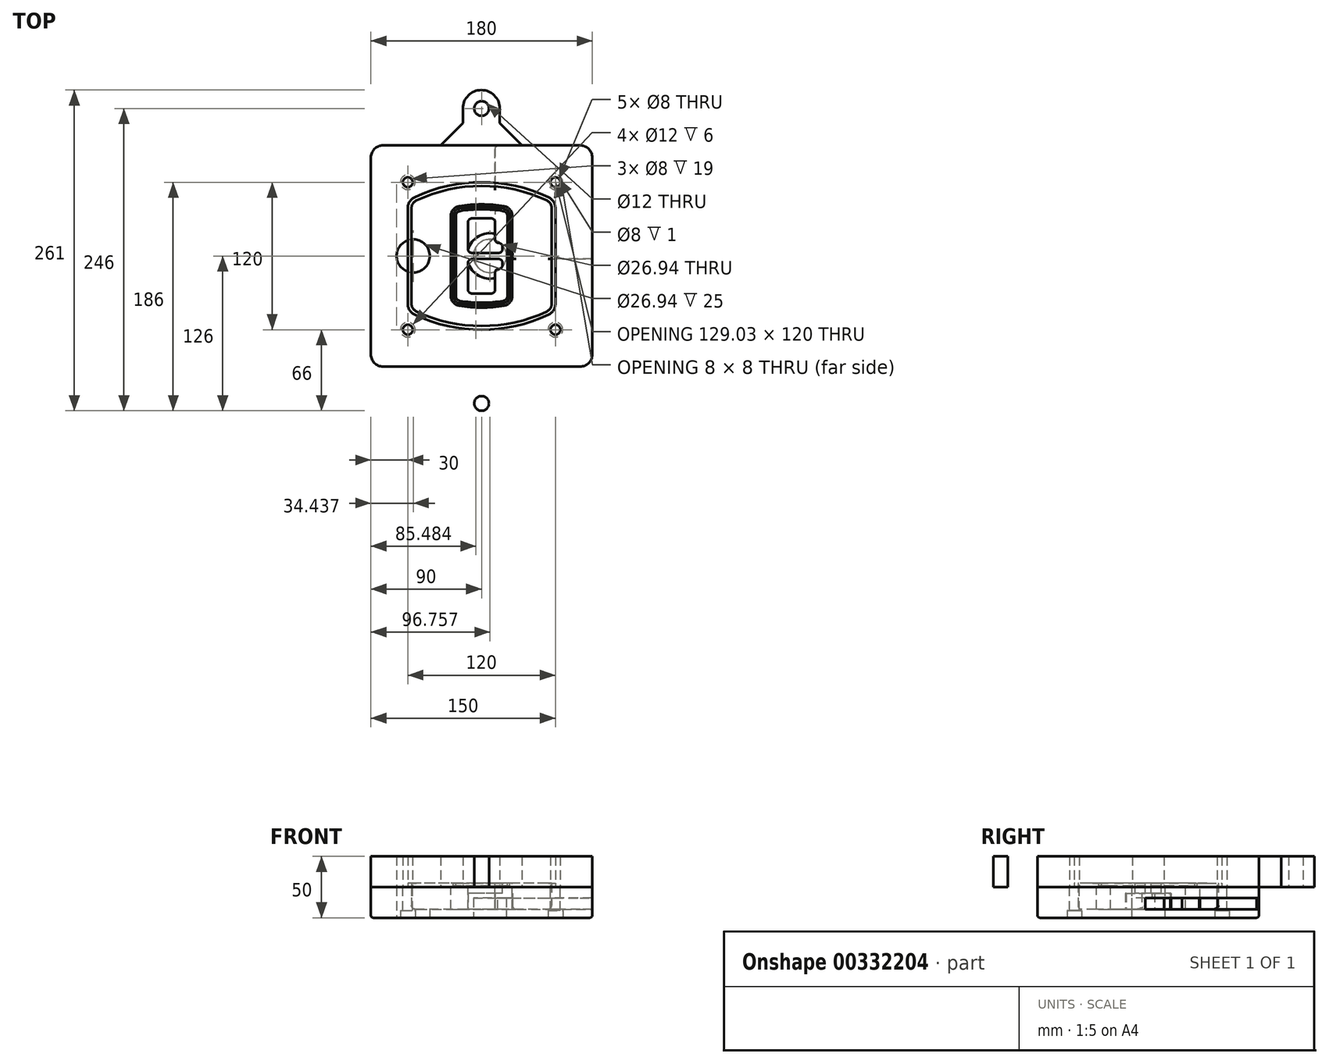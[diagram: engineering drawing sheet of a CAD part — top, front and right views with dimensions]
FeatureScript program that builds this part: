
annotation { "Feature Type Name" : "Feature", "Feature Type Description" : "" }
export const myFeature = defineFeature(function(context is Context, id is Id, definition is map)
    precondition{}
    {
        {
            var Q0;
            Q0=qCreatedBy(makeId("Top.planeOp"),FACE);
            var sketch = newSketch(context, id + "F0", { "sketchPlane" : qUnion([Q0])});
            skPoint(sketch, "E0.rect.middle", {"position": v(0, 0) * mm});
            skLineSegment(sketch, "E1.bottom", {"start": v(-80, -90) * mm, "end": v(80, -90) * mm});
            skLineSegment(sketch, "E1.top", {"start": v(-80, 90) * mm, "end": v(80, 90) * mm});
            skLineSegment(sketch, "E1.left", {"start": v(-90, -80) * mm, "end": v(-90, 80) * mm});
            skLineSegment(sketch, "E1.right", {"start": v(90, -80) * mm, "end": v(90, 80) * mm});
            skLineSegment(sketch, "E2", {"start": v(-90, 90) * mm, "end": v(90, -90) * mm, "construction": true});
            skLineSegment(sketch, "E3", {"start": v(90, 90) * mm, "end": v(-90, -90) * mm, "construction": true});
            skCircle(sketch, "E4", {"center": v(-60, 60) * mm, "radius": 4 * mm});
            skCircle(sketch, "E5", {"center": v(60, 60) * mm, "radius": 4 * mm});
            skCircle(sketch, "E6", {"center": v(60, -60) * mm, "radius": 4 * mm});
            skCircle(sketch, "E7", {"center": v(-60, -60) * mm, "radius": 4 * mm});
            skLineSegment(sketch, "E8", {"start": v(-60, 60) * mm, "end": v(60, 60) * mm, "construction": true});
            skLineSegment(sketch, "E9", {"start": v(60, 60) * mm, "end": v(60, -60) * mm, "construction": true});
            skLineSegment(sketch, "E10", {"start": v(60, -60) * mm, "end": v(-60, -60) * mm, "construction": true});
            skLineSegment(sketch, "E11", {"start": v(-60, -60) * mm, "end": v(-60, 60) * mm, "construction": true});
            skLineSegment(sketch, "E12", {"start": v(-60, 38.83) * mm, "end": v(-60, -38.83) * mm});
            skLineSegment(sketch, "E13", {"start": v(60, 38.83) * mm, "end": v(60, -38.83) * mm});
            skArc(sketch, "E14", {"start": v(54.26, 47.88) * mm, "mid": v(0, 60) * mm, "end": v(-54.26, 47.88) * mm});
            skArc(sketch, "E15", {"start": v(-54.26, -47.88) * mm, "mid": v(0, -60) * mm, "end": v(54.26, -47.88) * mm});
            skLineSegment(sketch, "E16", {"start": v(-60, 0) * mm, "end": v(60, 0) * mm, "construction": true});
            skPoint(sketch, "E17.visualSharp", {"position": v(-60, -45) * mm});
            skArc(sketch, "E17.filletArc", {"start": v(-60, -38.83) * mm, "mid": v(-58.44, -44.2) * mm, "end": v(-54.26, -47.88) * mm});
            skPoint(sketch, "E18.visualSharp", {"position": v(-60, 45) * mm});
            skArc(sketch, "E18.filletArc", {"start": v(-54.26, 47.88) * mm, "mid": v(-58.44, 44.2) * mm, "end": v(-60, 38.83) * mm});
            skPoint(sketch, "E19.visualSharp", {"position": v(60, 45) * mm});
            skArc(sketch, "E19.filletArc", {"start": v(60, 38.83) * mm, "mid": v(58.44, 44.2) * mm, "end": v(54.26, 47.88) * mm});
            skPoint(sketch, "E20.visualSharp", {"position": v(60, -45) * mm});
            skArc(sketch, "E20.filletArc", {"start": v(54.26, -47.88) * mm, "mid": v(58.44, -44.2) * mm, "end": v(60, -38.83) * mm});
            skPoint(sketch, "E21.visualSharp", {"position": v(-90, 90) * mm});
            skArc(sketch, "E21.filletArc", {"start": v(-80, 90) * mm, "mid": v(-87.07, 87.07) * mm, "end": v(-90, 80) * mm});
            skPoint(sketch, "E22.visualSharp", {"position": v(90, 90) * mm});
            skArc(sketch, "E22.filletArc", {"start": v(90, 80) * mm, "mid": v(87.07, 87.07) * mm, "end": v(80, 90) * mm});
            skPoint(sketch, "E23.visualSharp", {"position": v(90, -90) * mm});
            skArc(sketch, "E23.filletArc", {"start": v(80, -90) * mm, "mid": v(87.07, -87.07) * mm, "end": v(90, -80) * mm});
            skPoint(sketch, "E24.visualSharp", {"position": v(-90, -90) * mm});
            skArc(sketch, "E24.filletArc", {"start": v(-90, -80) * mm, "mid": v(-87.07, -87.07) * mm, "end": v(-80, -90) * mm});
            skArc(sketch, "E25.0", {"start": v(57, 38.83) * mm, "mid": v(55.9, 42.58) * mm, "end": v(52.98, 45.17) * mm});
            skLineSegment(sketch, "E25.1", {"start": v(57, 38.83) * mm, "end": v(57, -38.83) * mm});
            skArc(sketch, "E25.2", {"start": v(52.98, -45.17) * mm, "mid": v(55.9, -42.58) * mm, "end": v(57, -38.83) * mm});
            skArc(sketch, "E25.3", {"start": v(-52.98, -45.17) * mm, "mid": v(0, -57) * mm, "end": v(52.98, -45.17) * mm});
            skArc(sketch, "E25.4", {"start": v(-57, -38.83) * mm, "mid": v(-55.9, -42.58) * mm, "end": v(-52.98, -45.17) * mm});
            skArc(sketch, "E25.5", {"start": v(52.98, 45.17) * mm, "mid": v(0, 57) * mm, "end": v(-52.98, 45.17) * mm});
            skLineSegment(sketch, "E25.6", {"start": v(-57, 38.83) * mm, "end": v(-57, -38.83) * mm});
            skArc(sketch, "E25.7", {"start": v(-52.98, 45.17) * mm, "mid": v(-55.9, 42.58) * mm, "end": v(-57, 38.83) * mm});
            skArc(sketch, "E26.0", {"start": v(-55.96, 51.5) * mm, "mid": v(-61.82, 46.33) * mm, "end": v(-64, 38.83) * mm});
            skArc(sketch, "E26.1", {"start": v(55.96, 51.5) * mm, "mid": v(0, 64) * mm, "end": v(-55.96, 51.5) * mm});
            skArc(sketch, "E26.2", {"start": v(64, 38.83) * mm, "mid": v(61.82, 46.33) * mm, "end": v(55.96, 51.5) * mm});
            skLineSegment(sketch, "E26.3", {"start": v(64, 38.83) * mm, "end": v(64, -38.83) * mm});
            skArc(sketch, "E26.4", {"start": v(55.96, -51.5) * mm, "mid": v(61.82, -46.33) * mm, "end": v(64, -38.83) * mm});
            skLineSegment(sketch, "E26.5", {"start": v(-64, 38.83) * mm, "end": v(-64, -38.83) * mm});
            skArc(sketch, "E26.6", {"start": v(-55.96, -51.5) * mm, "mid": v(0, -64) * mm, "end": v(55.96, -51.5) * mm});
            skArc(sketch, "E26.7", {"start": v(-64, -38.83) * mm, "mid": v(-61.82, -46.33) * mm, "end": v(-55.96, -51.5) * mm});
            skSolve(sketch);
        }
        {
            var Q0;
            Q0=makeQuery(id+"F0.imprint","IMPRINT",FACE,{"disambiguationData":[TD([[makeQuery(id+"F0.imprint","IMPRINT",EDGE,{"derivedFrom":sQuery(id+"F0.wireOp",EDGE,"E1.bottom")}),1.0]])]});
            var Q1;
            Q1=makeQuery(id+"F0.imprint","IMPRINT",FACE,{"disambiguationData":[TD([[makeQuery(id+"F0.imprint","IMPRINT",EDGE,{"derivedFrom":sQuery(id+"F0.wireOp",EDGE,"E12")}),1.0]])]});
            var Q2;
            Q2=makeQuery(id+"F0.imprint","IMPRINT",FACE,{"disambiguationData":[TD([[makeQuery(id+"F0.imprint","IMPRINT",EDGE,{"derivedFrom":sQuery(id+"F0.wireOp",EDGE,"E25.0")}),1.0]])]});
            var Q3;
            Q3=makeQuery(id+"F0.imprint","IMPRINT",FACE,{"disambiguationData":[TD([[makeQuery(id+"F0.imprint","IMPRINT",EDGE,{"derivedFrom":sQuery(id+"F0.wireOp",EDGE,"E12")}),-1.0]])]});
            extrude(context, id + "F1", {"entities" : qUnion([Q0, Q1, Q2, Q3]), "oppositeDirection" : true, "depth" : 25 * mm});
        }
        {
            var Q0;
            Q0=makeQuery(id+"F0.imprint","IMPRINT",FACE,{"disambiguationData":[TD([[makeQuery(id+"F0.imprint","IMPRINT",EDGE,{"derivedFrom":sQuery(id+"F0.wireOp",EDGE,"E12")}),1.0]])]});
            extrude(context, id + "F2", {"entities" : qUnion([Q0]), "operationType" : NewBodyOperationType.ADD, "depth" : 3 * mm});
        }
        {
            var Q0;
            Q0=makeQuery(id+"F0.imprint","IMPRINT",FACE,{"disambiguationData":[TD([[makeQuery(id+"F0.imprint","IMPRINT",EDGE,{"derivedFrom":sQuery(id+"F0.wireOp",EDGE,"E25.0")}),1.0]])]});
            extrude(context, id + "F3", {"entities" : qUnion([Q0]), "operationType" : NewBodyOperationType.REMOVE, "oppositeDirection" : true, "depth" : 18 * mm});
        }
        {
            var Q0;
            Q0=makeQuery(id+"F2.opExtrude","CAP_FACE",FACE,{"disambiguationData":[OSD([sQuery(id+"F0.wireOp",EDGE,"E12"),sQuery(id+"F0.wireOp",EDGE,"E13"),sQuery(id+"F0.wireOp",EDGE,"E14"),sQuery(id+"F0.wireOp",EDGE,"E15"),sQuery(id+"F0.wireOp",EDGE,"E17.filletArc"),sQuery(id+"F0.wireOp",EDGE,"E18.filletArc"),sQuery(id+"F0.wireOp",EDGE,"E19.filletArc"),sQuery(id+"F0.wireOp",EDGE,"E20.filletArc"),sQuery(id+"F0.wireOp",EDGE,"E25.0"),sQuery(id+"F0.wireOp",EDGE,"E25.1"),sQuery(id+"F0.wireOp",EDGE,"E25.2"),sQuery(id+"F0.wireOp",EDGE,"E25.3"),sQuery(id+"F0.wireOp",EDGE,"E25.4"),sQuery(id+"F0.wireOp",EDGE,"E25.5"),sQuery(id+"F0.wireOp",EDGE,"E25.6"),sQuery(id+"F0.wireOp",EDGE,"E25.7")])],"isStart":false});
            var sketch = newSketch(context, id + "F4", { "sketchPlane" : qUnion([Q0])});
            skArc(sketch, "E27.0", {"start": v(-18.34, -40.45) * mm, "mid": v(0, -42) * mm, "end": v(18.34, -40.45) * mm});
            skArc(sketch, "E28.0", {"start": v(18.34, 40.45) * mm, "mid": v(0, 42) * mm, "end": v(-18.34, 40.45) * mm});
            skLineSegment(sketch, "E29", {"start": v(-25, 32.57) * mm, "end": v(-25, -32.57) * mm});
            skLineSegment(sketch, "E30", {"start": v(25, 32.57) * mm, "end": v(25, -32.57) * mm});
            skLineSegment(sketch, "E31", {"start": v(-25, 39.1) * mm, "end": v(25, 39.1) * mm, "construction": true});
            skLineSegment(sketch, "E32", {"start": v(-25, -39.1) * mm, "end": v(25, -39.1) * mm, "construction": true});
            skPoint(sketch, "E33.visualSharp", {"position": v(-25, 39.1) * mm});
            skArc(sketch, "E33.filletArc", {"start": v(-18.34, 40.45) * mm, "mid": v(-23.11, 37.73) * mm, "end": v(-25, 32.57) * mm});
            skPoint(sketch, "E34.visualSharp", {"position": v(25, 39.1) * mm});
            skArc(sketch, "E34.filletArc", {"start": v(25, 32.57) * mm, "mid": v(23.11, 37.73) * mm, "end": v(18.34, 40.45) * mm});
            skPoint(sketch, "E35.visualSharp", {"position": v(25, -39.1) * mm});
            skArc(sketch, "E35.filletArc", {"start": v(18.34, -40.45) * mm, "mid": v(23.11, -37.73) * mm, "end": v(25, -32.57) * mm});
            skPoint(sketch, "E36.visualSharp", {"position": v(-25, -39.1) * mm});
            skArc(sketch, "E36.filletArc", {"start": v(-25, -32.57) * mm, "mid": v(-23.11, -37.73) * mm, "end": v(-18.34, -40.45) * mm});
            skArc(sketch, "E37.0", {"start": v(52.98, 45.17) * mm, "mid": v(0, 57) * mm, "end": v(-52.98, 45.17) * mm});
            skArc(sketch, "E37.1", {"start": v(-52.98, 45.17) * mm, "mid": v(-55.9, 42.58) * mm, "end": v(-57, 38.83) * mm});
            skLineSegment(sketch, "E37.2", {"start": v(-57, 38.83) * mm, "end": v(-57, -38.83) * mm});
            skArc(sketch, "E37.3", {"start": v(-57, -38.83) * mm, "mid": v(-55.9, -42.58) * mm, "end": v(-52.98, -45.17) * mm});
            skArc(sketch, "E37.4", {"start": v(-52.98, -45.17) * mm, "mid": v(0, -57) * mm, "end": v(52.98, -45.17) * mm});
            skArc(sketch, "E37.5", {"start": v(52.98, -45.17) * mm, "mid": v(55.9, -42.58) * mm, "end": v(57, -38.83) * mm});
            skLineSegment(sketch, "E37.6", {"start": v(57, 38.83) * mm, "end": v(57, -38.83) * mm});
            skArc(sketch, "E37.7", {"start": v(57, 38.83) * mm, "mid": v(55.9, 42.58) * mm, "end": v(52.98, 45.17) * mm});
            skLineSegment(sketch, "E38.0", {"start": v(23, 32.57) * mm, "end": v(23, -32.57) * mm});
            skArc(sketch, "E38.1", {"start": v(18, -38.48) * mm, "mid": v(21.58, -36.44) * mm, "end": v(23, -32.57) * mm});
            skArc(sketch, "E38.2", {"start": v(-18, -38.48) * mm, "mid": v(0, -40) * mm, "end": v(18, -38.48) * mm});
            skArc(sketch, "E38.3", {"start": v(-23, -32.57) * mm, "mid": v(-21.58, -36.44) * mm, "end": v(-18, -38.48) * mm});
            skLineSegment(sketch, "E38.4", {"start": v(-23, 32.57) * mm, "end": v(-23, -32.57) * mm});
            skArc(sketch, "E38.5", {"start": v(23, 32.57) * mm, "mid": v(21.58, 36.44) * mm, "end": v(18, 38.48) * mm});
            skArc(sketch, "E38.6", {"start": v(-18, 38.48) * mm, "mid": v(-21.58, 36.44) * mm, "end": v(-23, 32.57) * mm});
            skArc(sketch, "E38.7", {"start": v(18, 38.48) * mm, "mid": v(0, 40) * mm, "end": v(-18, 38.48) * mm});
            skArc(sketch, "E39.0", {"start": v(21, 32.57) * mm, "mid": v(20.06, 35.15) * mm, "end": v(17.67, 36.5) * mm});
            skLineSegment(sketch, "E39.1", {"start": v(21, 32.57) * mm, "end": v(21, -32.57) * mm});
            skArc(sketch, "E39.2", {"start": v(17.67, -36.5) * mm, "mid": v(20.06, -35.15) * mm, "end": v(21, -32.57) * mm});
            skArc(sketch, "E39.3", {"start": v(-17.67, -36.5) * mm, "mid": v(0, -38) * mm, "end": v(17.67, -36.5) * mm});
            skArc(sketch, "E39.4", {"start": v(-21, -32.57) * mm, "mid": v(-20.06, -35.15) * mm, "end": v(-17.67, -36.5) * mm});
            skArc(sketch, "E39.5", {"start": v(17.67, 36.5) * mm, "mid": v(0, 38) * mm, "end": v(-17.67, 36.5) * mm});
            skLineSegment(sketch, "E39.6", {"start": v(-21, 32.57) * mm, "end": v(-21, -32.57) * mm});
            skArc(sketch, "E39.7", {"start": v(-17.67, 36.5) * mm, "mid": v(-20.06, 35.15) * mm, "end": v(-21, 32.57) * mm});
            skLineSegment(sketch, "E40", {"start": v(-25, 0) * mm, "end": v(25, 0) * mm, "construction": true});
            skLineSegment(sketch, "E41", {"start": v(-11, 5.5) * mm, "end": v(-11, 27.5) * mm});
            skLineSegment(sketch, "E42", {"start": v(-8, 30.5) * mm, "end": v(8, 30.5) * mm});
            skLineSegment(sketch, "E43", {"start": v(11, 27.5) * mm, "end": v(11, 13.5) * mm});
            skLineSegment(sketch, "E44", {"start": v(14, 10.5) * mm, "end": v(14, 10.5) * mm});
            skLineSegment(sketch, "E45", {"start": v(17, 7.5) * mm, "end": v(17, 5.5) * mm});
            skLineSegment(sketch, "E46", {"start": v(14, 2.5) * mm, "end": v(-8, 2.5) * mm});
            skPoint(sketch, "E47.visualSharp", {"position": v(-11, 30.5) * mm});
            skArc(sketch, "E47.filletArc", {"start": v(-8, 30.5) * mm, "mid": v(-10.12, 29.62) * mm, "end": v(-11, 27.5) * mm});
            skPoint(sketch, "E48.visualSharp", {"position": v(11, 30.5) * mm});
            skArc(sketch, "E48.filletArc", {"start": v(11, 27.5) * mm, "mid": v(10.12, 29.62) * mm, "end": v(8, 30.5) * mm});
            skPoint(sketch, "E49.visualSharp", {"position": v(11, 10.5) * mm});
            skArc(sketch, "E49.filletArc", {"start": v(11, 13.5) * mm, "mid": v(11.88, 11.38) * mm, "end": v(14, 10.5) * mm});
            skPoint(sketch, "E50.visualSharp", {"position": v(17, 10.5) * mm});
            skArc(sketch, "E50.filletArc", {"start": v(17, 7.5) * mm, "mid": v(16.12, 9.62) * mm, "end": v(14, 10.5) * mm});
            skPoint(sketch, "E51.visualSharp", {"position": v(17, 2.5) * mm});
            skArc(sketch, "E51.filletArc", {"start": v(14, 2.5) * mm, "mid": v(16.12, 3.38) * mm, "end": v(17, 5.5) * mm});
            skPoint(sketch, "E52.visualSharp", {"position": v(-11, 2.5) * mm});
            skArc(sketch, "E52.filletArc", {"start": v(-11, 5.5) * mm, "mid": v(-10.12, 3.38) * mm, "end": v(-8, 2.5) * mm});
            skLineSegment(sketch, "E53.0.MirrorCS", {"start": v(14, -2.5) * mm, "end": v(-8, -2.5) * mm});
            skArc(sketch, "E54.0.MirrorCS", {"start": v(-11, -5.5) * mm, "mid": v(-10.12, -3.38) * mm, "end": v(-8, -2.5) * mm});
            skLineSegment(sketch, "E55.0.MirrorCS", {"start": v(-11, -5.5) * mm, "end": v(-11, -27.5) * mm});
            skArc(sketch, "E56.0.MirrorCS", {"start": v(-8, -30.5) * mm, "mid": v(-10.12, -29.62) * mm, "end": v(-11, -27.5) * mm});
            skLineSegment(sketch, "E57.0.MirrorCS", {"start": v(-8, -30.5) * mm, "end": v(8, -30.5) * mm});
            skArc(sketch, "E58.0.MirrorCS", {"start": v(11, -27.5) * mm, "mid": v(10.12, -29.62) * mm, "end": v(8, -30.5) * mm});
            skLineSegment(sketch, "E59.0.MirrorCS", {"start": v(11, -27.5) * mm, "end": v(11, -13.5) * mm});
            skArc(sketch, "E60.0.MirrorCS", {"start": v(11, -13.5) * mm, "mid": v(11.88, -11.38) * mm, "end": v(14, -10.5) * mm});
            skArc(sketch, "E61.0.MirrorCS", {"start": v(17, -7.5) * mm, "mid": v(16.12, -9.62) * mm, "end": v(14, -10.5) * mm});
            skLineSegment(sketch, "E62.0.MirrorCS", {"start": v(17, -7.5) * mm, "end": v(17, -5.5) * mm});
            skArc(sketch, "E63.0.MirrorCS", {"start": v(14, -2.5) * mm, "mid": v(16.12, -3.38) * mm, "end": v(17, -5.5) * mm});
            skSolve(sketch);
        }
        {
            var Q0;
            Q0=makeQuery(id+"F4.imprint","IMPRINT",FACE,{"disambiguationData":[TD([[makeQuery(id+"F4.imprint","IMPRINT",EDGE,{"derivedFrom":sQuery(id+"F4.wireOp",EDGE,"E27.0")}),1.0]])]});
            var Q1;
            Q1=makeQuery(id+"F4.imprint","IMPRINT",FACE,{"disambiguationData":[TD([[makeQuery(id+"F4.imprint","IMPRINT",EDGE,{"derivedFrom":sQuery(id+"F4.wireOp",EDGE,"E38.0")}),-1.0]])]});
            var Q2;
            Q2=makeQuery(id+"F4.imprint","IMPRINT",FACE,{"disambiguationData":[TD([[makeQuery(id+"F4.imprint","IMPRINT",EDGE,{"derivedFrom":sQuery(id+"F4.wireOp",EDGE,"E39.0")}),1.0]])]});
            extrude(context, id + "F5", {"entities" : qUnion([Q0, Q1, Q2]), "operationType" : NewBodyOperationType.ADD, "endBound" : BoundingType.UP_TO_NEXT, "oppositeDirection" : true, "depth" : 25 * mm});
        }
        {
            var Q0;
            Q0=makeQuery(id+"F4.imprint","IMPRINT",FACE,{"disambiguationData":[TD([[makeQuery(id+"F4.imprint","IMPRINT",EDGE,{"derivedFrom":sQuery(id+"F4.wireOp",EDGE,"E38.0")}),-1.0]])]});
            extrude(context, id + "F6", {"entities" : qUnion([Q0]), "operationType" : NewBodyOperationType.REMOVE, "oppositeDirection" : true, "depth" : 2 * mm});
        }
        {
            var Q0;
            Q0=makeQuery(id+"F1.opExtrude","CAP_FACE",FACE,{"disambiguationData":[OSD([sQuery(id+"F0.wireOp",EDGE,"E1.bottom"),sQuery(id+"F0.wireOp",EDGE,"E1.top"),sQuery(id+"F0.wireOp",EDGE,"E1.left"),sQuery(id+"F0.wireOp",EDGE,"E1.right"),sQuery(id+"F0.wireOp",EDGE,"E4"),sQuery(id+"F0.wireOp",EDGE,"E5"),sQuery(id+"F0.wireOp",EDGE,"E6"),sQuery(id+"F0.wireOp",EDGE,"E7"),sQuery(id+"F0.wireOp",EDGE,"E21.filletArc"),sQuery(id+"F0.wireOp",EDGE,"E22.filletArc"),sQuery(id+"F0.wireOp",EDGE,"E23.filletArc"),sQuery(id+"F0.wireOp",EDGE,"E24.filletArc")])],"isStart":false});
            var sketch = newSketch(context, id + "F7", { "sketchPlane" : qUnion([Q0])});
            skCircle(sketch, "E64", {"center": v(6.76, 0) * mm, "radius": 13.47 * mm});
            skCircle(sketch, "E65", {"center": v(-55.56, 0) * mm, "radius": 13.47 * mm});
            skLineSegment(sketch, "E66", {"start": v(90, 0) * mm, "end": v(-90, 0) * mm});
            skCircle(sketch, "E67", {"center": v(6.76, 0) * mm, "radius": 18.47 * mm});
            skCircle(sketch, "E68", {"center": v(60, -60) * mm, "radius": 6 * mm});
            skCircle(sketch, "E69", {"center": v(-60, -60) * mm, "radius": 6 * mm});
            skCircle(sketch, "E70", {"center": v(-60, 60) * mm, "radius": 6 * mm});
            skCircle(sketch, "E71", {"center": v(60, 60) * mm, "radius": 6 * mm});
            skSolve(sketch);
        }
        {
            var Q0;
            {var subQ1=sQuery(id+"F7.wireOp",EDGE,"E66");var subQ4=sQuery(id+"F7.wireOp",EDGE,"E64");var subQ6=makeQuery(id+"F7.imprint","INTERSECT",VERTEX,{"disambiguationData":[OD(0.0)],"derivedFrom":[subQ4,subQ1]});Q0=makeQuery(id+"F7.imprint","IMPRINT",FACE,{"disambiguationData":[TD([[makeQuery(id+"F7.imprint","IMPRINT",EDGE,{"disambiguationData":[TD([[subQ6,-1.0]])],"derivedFrom":subQ4}),-1.0]])]});}
            var Q1;
            {var subQ0=sQuery(id+"F7.wireOp",EDGE,"E66");var subQ1=sQuery(id+"F7.wireOp",EDGE,"E64");var subQ3=makeQuery(id+"F7.imprint","INTERSECT",VERTEX,{"disambiguationData":[OD(0.0)],"derivedFrom":[subQ1,subQ0]});Q1=makeQuery(id+"F7.imprint","IMPRINT",FACE,{"disambiguationData":[TD([[makeQuery(id+"F7.imprint","IMPRINT",EDGE,{"disambiguationData":[TD([[subQ3,-1.0]])],"derivedFrom":subQ1}),1.0]])]});}
            var Q2;
            {var subQ0=sQuery(id+"F7.wireOp",EDGE,"E66");var subQ1=sQuery(id+"F7.wireOp",EDGE,"E64");var subQ3=makeQuery(id+"F7.imprint","INTERSECT",VERTEX,{"disambiguationData":[OD(0.0)],"derivedFrom":[subQ1,subQ0]});Q2=makeQuery(id+"F7.imprint","IMPRINT",FACE,{"disambiguationData":[TD([[makeQuery(id+"F7.imprint","IMPRINT",EDGE,{"disambiguationData":[TD([[subQ3,1.0]])],"derivedFrom":subQ1}),1.0]])]});}
            var Q3;
            {var subQ1=sQuery(id+"F7.wireOp",EDGE,"E66");var subQ4=sQuery(id+"F7.wireOp",EDGE,"E64");var subQ6=makeQuery(id+"F7.imprint","INTERSECT",VERTEX,{"disambiguationData":[OD(0.0)],"derivedFrom":[subQ4,subQ1]});Q3=makeQuery(id+"F7.imprint","IMPRINT",FACE,{"disambiguationData":[TD([[makeQuery(id+"F7.imprint","IMPRINT",EDGE,{"disambiguationData":[TD([[subQ6,1.0]])],"derivedFrom":subQ4}),-1.0]])]});}
            extrude(context, id + "F8", {"entities" : qUnion([Q0, Q1, Q2, Q3]), "operationType" : NewBodyOperationType.ADD, "oppositeDirection" : true, "depth" : 20 * mm});
        }
        {
            var Q0;
            {var subQ0=sQuery(id+"F7.wireOp",EDGE,"E66");var subQ1=sQuery(id+"F7.wireOp",EDGE,"E64");var subQ3=makeQuery(id+"F7.imprint","INTERSECT",VERTEX,{"disambiguationData":[OD(0.0)],"derivedFrom":[subQ1,subQ0]});Q0=makeQuery(id+"F7.imprint","IMPRINT",FACE,{"disambiguationData":[TD([[makeQuery(id+"F7.imprint","IMPRINT",EDGE,{"disambiguationData":[TD([[subQ3,-1.0]])],"derivedFrom":subQ1}),1.0]])]});}
            var Q1;
            {var subQ0=sQuery(id+"F7.wireOp",EDGE,"E66");var subQ1=sQuery(id+"F7.wireOp",EDGE,"E64");var subQ3=makeQuery(id+"F7.imprint","INTERSECT",VERTEX,{"disambiguationData":[OD(0.0)],"derivedFrom":[subQ1,subQ0]});Q1=makeQuery(id+"F7.imprint","IMPRINT",FACE,{"disambiguationData":[TD([[makeQuery(id+"F7.imprint","IMPRINT",EDGE,{"disambiguationData":[TD([[subQ3,1.0]])],"derivedFrom":subQ1}),1.0]])]});}
            extrude(context, id + "F9", {"entities" : qUnion([Q0, Q1]), "operationType" : NewBodyOperationType.REMOVE, "oppositeDirection" : true, "depth" : 16 * mm});
        }
        {
            var Q0;
            {var subQ0=sQuery(id+"F7.wireOp",EDGE,"E66");var subQ1=sQuery(id+"F7.wireOp",EDGE,"E65");var subQ3=makeQuery(id+"F7.imprint","INTERSECT",VERTEX,{"disambiguationData":[OD(0.0)],"derivedFrom":[subQ1,subQ0]});Q0=makeQuery(id+"F7.imprint","IMPRINT",FACE,{"disambiguationData":[TD([[makeQuery(id+"F7.imprint","IMPRINT",EDGE,{"disambiguationData":[TD([[subQ3,-1.0]])],"derivedFrom":subQ1}),1.0]])]});}
            var Q1;
            {var subQ0=sQuery(id+"F7.wireOp",EDGE,"E66");var subQ1=sQuery(id+"F7.wireOp",EDGE,"E65");var subQ3=makeQuery(id+"F7.imprint","INTERSECT",VERTEX,{"disambiguationData":[OD(0.0)],"derivedFrom":[subQ1,subQ0]});Q1=makeQuery(id+"F7.imprint","IMPRINT",FACE,{"disambiguationData":[TD([[makeQuery(id+"F7.imprint","IMPRINT",EDGE,{"disambiguationData":[TD([[subQ3,1.0]])],"derivedFrom":subQ1}),1.0]])]});}
            extrude(context, id + "F10", {"entities" : qUnion([Q0, Q1]), "operationType" : NewBodyOperationType.REMOVE, "oppositeDirection" : true, "depth" : 25 * mm});
        }
        {
            var Q0;
            Q0=makeQuery(id+"F7.imprint","IMPRINT",FACE,{"disambiguationData":[TD([[makeQuery(id+"F7.imprint","IMPRINT",EDGE,{"derivedFrom":sQuery(id+"F7.wireOp",EDGE,"E68")}),1.0]])]});
            var Q1;
            Q1=makeQuery(id+"F7.imprint","IMPRINT",FACE,{"disambiguationData":[TD([[makeQuery(id+"F7.imprint","IMPRINT",EDGE,{"derivedFrom":makeQuery(id+"F1.opExtrude","CAP_EDGE",EDGE,{"disambiguationData":[OSD([sQuery(id+"F0.wireOp",EDGE,"E5")])],"isStart":false})}),-1.0]])]});
            var Q2;
            Q2=makeQuery(id+"F7.imprint","IMPRINT",FACE,{"disambiguationData":[TD([[makeQuery(id+"F7.imprint","IMPRINT",EDGE,{"derivedFrom":sQuery(id+"F7.wireOp",EDGE,"E69")}),1.0]])]});
            var Q3;
            Q3=makeQuery(id+"F7.imprint","IMPRINT",FACE,{"disambiguationData":[TD([[makeQuery(id+"F7.imprint","IMPRINT",EDGE,{"derivedFrom":makeQuery(id+"F1.opExtrude","CAP_EDGE",EDGE,{"disambiguationData":[OSD([sQuery(id+"F0.wireOp",EDGE,"E4")])],"isStart":false})}),-1.0]])]});
            var Q4;
            Q4=makeQuery(id+"F7.imprint","IMPRINT",FACE,{"disambiguationData":[TD([[makeQuery(id+"F7.imprint","IMPRINT",EDGE,{"derivedFrom":sQuery(id+"F7.wireOp",EDGE,"E70")}),1.0]])]});
            var Q5;
            Q5=makeQuery(id+"F7.imprint","IMPRINT",FACE,{"disambiguationData":[TD([[makeQuery(id+"F7.imprint","IMPRINT",EDGE,{"derivedFrom":makeQuery(id+"F1.opExtrude","CAP_EDGE",EDGE,{"disambiguationData":[OSD([sQuery(id+"F0.wireOp",EDGE,"E7")])],"isStart":false})}),-1.0]])]});
            var Q6;
            Q6=makeQuery(id+"F7.imprint","IMPRINT",FACE,{"disambiguationData":[TD([[makeQuery(id+"F7.imprint","IMPRINT",EDGE,{"derivedFrom":sQuery(id+"F7.wireOp",EDGE,"E71")}),1.0]])]});
            var Q7;
            Q7=makeQuery(id+"F7.imprint","IMPRINT",FACE,{"disambiguationData":[TD([[makeQuery(id+"F7.imprint","IMPRINT",EDGE,{"derivedFrom":makeQuery(id+"F1.opExtrude","CAP_EDGE",EDGE,{"disambiguationData":[OSD([sQuery(id+"F0.wireOp",EDGE,"E6")])],"isStart":false})}),-1.0]])]});
            extrude(context, id + "F11", {"entities" : qUnion([Q0, Q1, Q2, Q3, Q4, Q5, Q6, Q7]), "operationType" : NewBodyOperationType.REMOVE, "oppositeDirection" : true, "depth" : 6 * mm});
        }
        {
            var Q0;
            Q0=makeQuery(id+"F9.boolean.opBoolean","COPY",FACE,{"derivedFrom":makeQuery(id+"F9.opExtrude","CAP_FACE",FACE,{"disambiguationData":[OSD([sQuery(id+"F7.wireOp",EDGE,"E64")])],"isStart":false})});
            var sketch = newSketch(context, id + "F12", { "sketchPlane" : qUnion([Q0])});
            skArc(sketch, "E72.0", {"start": v(11, -88.19) * mm, "mid": v(97.1, -83.6) * mm, "end": v(92.5, 2.5) * mm});
            skLineSegment(sketch, "E72.1", {"start": v(11, -17.97) * mm, "end": v(11, -17.97) * mm});
            skLineSegment(sketch, "E73", {"start": v(92.5, -105.13) * mm, "end": v(102.3, -105.13) * mm});
            skLineSegment(sketch, "E74.0", {"start": v(92.5, 2.5) * mm, "end": v(14, 2.5) * mm});
            skArc(sketch, "E74.1", {"start": v(14, 2.5) * mm, "mid": v(16.12, 3.38) * mm, "end": v(17, 5.5) * mm});
            skLineSegment(sketch, "E74.2", {"start": v(17, 7.5) * mm, "end": v(17, 5.5) * mm});
            skArc(sketch, "E74.3", {"start": v(17, 7.5) * mm, "mid": v(16.12, 9.62) * mm, "end": v(14, 10.5) * mm});
            skArc(sketch, "E74.4", {"start": v(11, 13.5) * mm, "mid": v(11.88, 11.38) * mm, "end": v(14, 10.5) * mm});
            skLineSegment(sketch, "E74.5", {"start": v(11, 13.5) * mm, "end": v(11, -88.19) * mm});
            skLineSegment(sketch, "E74.7", {"start": v(92.5, -2.5) * mm, "end": v(14, -2.5) * mm});
            skArc(sketch, "E74.8", {"start": v(14, -2.5) * mm, "mid": v(16.12, -3.38) * mm, "end": v(17, -5.5) * mm});
            skLineSegment(sketch, "E74.9", {"start": v(17, -7.5) * mm, "end": v(17, -5.5) * mm});
            skArc(sketch, "E74.10", {"start": v(17, -7.5) * mm, "mid": v(16.12, -9.62) * mm, "end": v(14, -10.5) * mm});
            skArc(sketch, "E74.11", {"start": v(11, -13.5) * mm, "mid": v(11.88, -11.38) * mm, "end": v(14, -10.5) * mm});
            skLineSegment(sketch, "E74.12", {"start": v(11, -17.97) * mm, "end": v(11, -13.5) * mm});
            skPoint(sketch, "E75.orphan", {"position": v(11, -27.5) * mm});
            skPoint(sketch, "E76.orphan", {"position": v(-8, -2.5) * mm});
            skPoint(sketch, "E77.orphan", {"position": v(-8, 2.5) * mm});
            skPoint(sketch, "E78.orphan", {"position": v(11, 27.5) * mm});
            skSolve(sketch);
        }
        {
            var Q0;
            {var subQ7=sQuery(id+"F12.wireOp",EDGE,"E72.0");var subQ14=sQuery(id+"F12.wireOp",EDGE,"E72.1");var subQ16=sQuery(id+"F12.wireOp",EDGE,"E74.1");var subQ18=sQuery(id+"F12.wireOp",EDGE,"E74.8");Q0=qUnion([makeQuery(id+"F12.imprint","IMPRINT",FACE,{"disambiguationData":[TD([[makeQuery(id+"F12.imprint","IMPRINT",EDGE,{"derivedFrom":subQ7}),1.0]])]}),makeQuery(id+"F12.imprint","IMPRINT",FACE,{"disambiguationData":[TD([[makeQuery(id+"F12.imprint","IMPRINT",EDGE,{"derivedFrom":subQ14}),1.0]])]}),makeQuery(id+"F12.imprint","IMPRINT",FACE,{"disambiguationData":[TD([[makeQuery(id+"F12.imprint","IMPRINT",EDGE,{"derivedFrom":subQ16}),1.0]])]}),makeQuery(id+"F12.imprint","IMPRINT",FACE,{"disambiguationData":[TD([[makeQuery(id+"F12.imprint","IMPRINT",EDGE,{"derivedFrom":subQ18}),-1.0]])]})]);}
            var Q1;
            Q1=makeQuery(id+"F5.boolean.opBoolean","SPLIT",FACE,{"disambiguationData":[TD([makeQuery(id+"F5.opExtrude","SWEPT_FACE",FACE,{"disambiguationData":[OSD([sQuery(id+"F4.wireOp",EDGE,"E41")])]})])],"derivedFrom":makeQuery(id+"F3.boolean.opBoolean","COPY",FACE,{"derivedFrom":makeQuery(id+"F3.opExtrude","CAP_FACE",FACE,{"disambiguationData":[OSD([sQuery(id+"F0.wireOp",EDGE,"E25.0"),sQuery(id+"F0.wireOp",EDGE,"E25.1"),sQuery(id+"F0.wireOp",EDGE,"E25.2"),sQuery(id+"F0.wireOp",EDGE,"E25.3"),sQuery(id+"F0.wireOp",EDGE,"E25.4"),sQuery(id+"F0.wireOp",EDGE,"E25.5"),sQuery(id+"F0.wireOp",EDGE,"E25.6"),sQuery(id+"F0.wireOp",EDGE,"E25.7")])],"isStart":false})})});
            extrude(context, id + "F13", {"entities" : qUnion([Q0]), "operationType" : NewBodyOperationType.REMOVE, "endBound" : BoundingType.UP_TO_SURFACE, "endBoundEntityFace" : qUnion([Q1]), "depth" : 25 * mm});
        }
        {
            var Q0;
            Q0=makeQuery(id+"F3.boolean.opBoolean","COPY",EDGE,{"derivedFrom":makeQuery(id+"F3.opExtrude","CAP_EDGE",EDGE,{"disambiguationData":[OSD([sQuery(id+"F0.wireOp",EDGE,"E25.6")])],"isStart":false})});
            var Q1;
            Q1=makeQuery(id+"F8.boolean.opBoolean","INTERSECT",EDGE,{"derivedFrom":[makeQuery(id+"F5.opExtrude","SWEPT_FACE",FACE,{"disambiguationData":[OSD([sQuery(id+"F4.wireOp",EDGE,"E30")])]}),makeQuery(id+"F8.opExtrude","CAP_FACE",FACE,{"disambiguationData":[OSD([sQuery(id+"F7.wireOp",EDGE,"E67")])],"isStart":false})]});
            var Q2;
            Q2=makeQuery(id+"F8.boolean.opBoolean","INTERSECT",EDGE,{"disambiguationData":[OD(1.0)],"derivedFrom":[makeQuery(id+"F5.opExtrude","SWEPT_FACE",FACE,{"disambiguationData":[OSD([sQuery(id+"F4.wireOp",EDGE,"E30")])]}),makeQuery(id+"F8.opExtrude","SWEPT_FACE",FACE,{"disambiguationData":[OSD([sQuery(id+"F7.wireOp",EDGE,"E67")])]})]});
            var Q3;
            {var subQ0=makeQuery(id+"F3.boolean.opBoolean","COPY",FACE,{"derivedFrom":makeQuery(id+"F3.opExtrude","CAP_FACE",FACE,{"disambiguationData":[OSD([sQuery(id+"F0.wireOp",EDGE,"E25.0"),sQuery(id+"F0.wireOp",EDGE,"E25.1"),sQuery(id+"F0.wireOp",EDGE,"E25.2"),sQuery(id+"F0.wireOp",EDGE,"E25.3"),sQuery(id+"F0.wireOp",EDGE,"E25.4"),sQuery(id+"F0.wireOp",EDGE,"E25.5"),sQuery(id+"F0.wireOp",EDGE,"E25.6"),sQuery(id+"F0.wireOp",EDGE,"E25.7")])],"isStart":false})});var subQ1=sQuery(id+"F4.wireOp",EDGE,"E30");Q3=makeQuery(id+"F8.boolean.opBoolean","SPLIT",EDGE,{"disambiguationData":[TD([makeQuery(id+"F5.opExtrude","SWEPT_FACE",FACE,{"disambiguationData":[OSD([sQuery(id+"F4.wireOp",EDGE,"E35.filletArc")])]})])],"derivedFrom":makeQuery(id+"F5.opExtrude","TWEAK_EDGE",EDGE,{"derivedFrom":[subQ0,makeQuery(id+"F4.imprint","IMPRINT",EDGE,{"derivedFrom":subQ1})]})});}
            var Q4;
            {var subQ0=sQuery(id+"F0.wireOp",EDGE,"E25.0");var subQ1=sQuery(id+"F0.wireOp",EDGE,"E25.1");var subQ2=sQuery(id+"F0.wireOp",EDGE,"E25.2");var subQ3=sQuery(id+"F0.wireOp",EDGE,"E25.3");var subQ4=sQuery(id+"F0.wireOp",EDGE,"E25.4");var subQ5=sQuery(id+"F0.wireOp",EDGE,"E25.5");var subQ6=sQuery(id+"F0.wireOp",EDGE,"E25.6");var subQ7=sQuery(id+"F0.wireOp",EDGE,"E25.7");Q4=makeQuery(id+"F8.boolean.opBoolean","INTERSECT",EDGE,{"derivedFrom":[makeQuery(id+"F5.boolean.opBoolean","SPLIT",FACE,{"disambiguationData":[TD([makeQuery(id+"F2.opExtrude","SWEPT_FACE",FACE,{"disambiguationData":[OSD([subQ0])]})])],"derivedFrom":makeQuery(id+"F3.boolean.opBoolean","COPY",FACE,{"derivedFrom":makeQuery(id+"F3.opExtrude","CAP_FACE",FACE,{"disambiguationData":[OSD([subQ0,subQ1,subQ2,subQ3,subQ4,subQ5,subQ6,subQ7])],"isStart":false})})}),makeQuery(id+"F8.opExtrude","SWEPT_FACE",FACE,{"disambiguationData":[OSD([sQuery(id+"F7.wireOp",EDGE,"E67")])]})]});}
            var Q5;
            Q5=makeQuery(id+"F8.boolean.opBoolean","INTERSECT",EDGE,{"disambiguationData":[OD(0.0)],"derivedFrom":[makeQuery(id+"F5.opExtrude","SWEPT_FACE",FACE,{"disambiguationData":[OSD([sQuery(id+"F4.wireOp",EDGE,"E30")])]}),makeQuery(id+"F8.opExtrude","SWEPT_FACE",FACE,{"disambiguationData":[OSD([sQuery(id+"F7.wireOp",EDGE,"E67")])]})]});
            fillet(context, id + "F14", {"entities" : qUnion([Q0, Q1, Q2, Q3, Q4, Q5]), "radius" : 3 * mm, "tangentPropagation" : true, "allowEdgeOverflow" : false});
        }
        {
            var Q0;
            Q0=makeQuery(id+"F1.opExtrude","CAP_EDGE",EDGE,{"disambiguationData":[OSD([sQuery(id+"F0.wireOp",EDGE,"E1.bottom")])],"isStart":false});
            fillet(context, id + "F15", {"entities" : qUnion([Q0]), "radius" : 2 * mm, "tangentPropagation" : true, "allowEdgeOverflow" : false});
        }
        {
            var Q0;
            {var subQ0=sQuery(id+"F0.wireOp",EDGE,"E21.filletArc");var subQ1=sQuery(id+"F0.wireOp",EDGE,"E7");var subQ2=sQuery(id+"F0.wireOp",EDGE,"E6");var subQ3=sQuery(id+"F0.wireOp",EDGE,"E5");var subQ4=sQuery(id+"F0.wireOp",EDGE,"E4");var subQ5=sQuery(id+"F0.wireOp",EDGE,"E22.filletArc");var subQ6=sQuery(id+"F0.wireOp",EDGE,"E1.bottom");var subQ7=sQuery(id+"F0.wireOp",EDGE,"E1.right");var subQ8=sQuery(id+"F0.wireOp",EDGE,"E1.top");var subQ9=sQuery(id+"F0.wireOp",EDGE,"E1.left");var subQ10=sQuery(id+"F0.wireOp",EDGE,"E23.filletArc");var subQ11=sQuery(id+"F0.wireOp",EDGE,"E24.filletArc");Q0=makeQuery(id+"F2.boolean.opBoolean","SPLIT",FACE,{"disambiguationData":[TD([makeQuery(id+"F1.opExtrude","SWEPT_FACE",FACE,{"disambiguationData":[OSD([subQ6])]})])],"derivedFrom":makeQuery(id+"F1.opExtrude","CAP_FACE",FACE,{"disambiguationData":[OSD([subQ6,subQ8,subQ9,subQ7,subQ4,subQ3,subQ2,subQ1,subQ0,subQ5,subQ10,subQ11])],"isStart":true})});}
            var sketch = newSketch(context, id + "F16", { "sketchPlane" : qUnion([Q0])});
            skLineSegment(sketch, "E79", {"start": v(0, 90) * mm, "end": v(0, 120) * mm, "construction": true});
            skCircle(sketch, "E80", {"center": v(0, 120) * mm, "radius": 6 * mm});
            skArc(sketch, "E81", {"start": v(14.79, 120) * mm, "mid": v(-0.21, 135) * mm, "end": v(-15.21, 120) * mm});
            skLineSegment(sketch, "E82", {"start": v(-15.21, 120) * mm, "end": v(-15.21, 108) * mm});
            skLineSegment(sketch, "E83", {"start": v(14.79, 120) * mm, "end": v(14.79, 108) * mm});
            skLineSegment(sketch, "E84", {"start": v(-15.21, 108) * mm, "end": v(-33.21, 90) * mm});
            skLineSegment(sketch, "E85", {"start": v(14.79, 108) * mm, "end": v(32.79, 90) * mm});
            skLineSegment(sketch, "E86", {"start": v(-90, 0) * mm, "end": v(90, 0) * mm, "construction": true});
            skLineSegment(sketch, "E87.MirrorCS", {"start": v(0, -90) * mm, "end": v(0, -120) * mm, "construction": true});
            skCircle(sketch, "E88.MirrorC", {"center": v(0, -120) * mm, "radius": 6 * mm});
            skArc(sketch, "E89.MirrorCS", {"start": v(14.79, -120) * mm, "mid": v(-0.21, -135) * mm, "end": v(-15.21, -120) * mm});
            skLineSegment(sketch, "E90.MirrorCS", {"start": v(-15.21, -120) * mm, "end": v(-15.21, -108) * mm});
            skLineSegment(sketch, "E91.MirrorCS", {"start": v(14.79, -120) * mm, "end": v(14.79, -108) * mm});
            skLineSegment(sketch, "E92.MirrorCS", {"start": v(-15.21, -108) * mm, "end": v(-33.21, -90) * mm});
            skLineSegment(sketch, "E93.MirrorCS", {"start": v(14.79, -108) * mm, "end": v(32.79, -90) * mm});
            skSolve(sketch);
        }
        {
            var Q0;
            {var subQ0=sQuery(id+"F0.wireOp",EDGE,"E21.filletArc");var subQ1=sQuery(id+"F0.wireOp",EDGE,"E7");var subQ2=sQuery(id+"F0.wireOp",EDGE,"E6");var subQ3=sQuery(id+"F0.wireOp",EDGE,"E5");var subQ4=sQuery(id+"F0.wireOp",EDGE,"E4");var subQ5=sQuery(id+"F0.wireOp",EDGE,"E22.filletArc");var subQ6=sQuery(id+"F0.wireOp",EDGE,"E1.bottom");var subQ7=sQuery(id+"F0.wireOp",EDGE,"E1.right");var subQ8=sQuery(id+"F0.wireOp",EDGE,"E1.top");var subQ9=sQuery(id+"F0.wireOp",EDGE,"E1.left");var subQ10=sQuery(id+"F0.wireOp",EDGE,"E23.filletArc");var subQ11=sQuery(id+"F0.wireOp",EDGE,"E24.filletArc");Q0=makeQuery(id+"F2.boolean.opBoolean","SPLIT",FACE,{"disambiguationData":[TD([makeQuery(id+"F1.opExtrude","SWEPT_FACE",FACE,{"disambiguationData":[OSD([subQ6])]})])],"derivedFrom":makeQuery(id+"F1.opExtrude","CAP_FACE",FACE,{"disambiguationData":[OSD([subQ6,subQ8,subQ9,subQ7,subQ4,subQ3,subQ2,subQ1,subQ0,subQ5,subQ10,subQ11])],"isStart":true})});}
            var Q1;
            Q1=makeQuery(id+"F16.imprint","IMPRINT",FACE,{"disambiguationData":[TD([[makeQuery(id+"F16.imprint","IMPRINT",EDGE,{"derivedFrom":sQuery(id+"F16.wireOp",EDGE,"E80")}),-1.0]])]});
            var Q2;
            Q2=makeQuery(id+"F16.imprint","IMPRINT",FACE,{"disambiguationData":[TD([[makeQuery(id+"F16.imprint","IMPRINT",EDGE,{"derivedFrom":sQuery(id+"F16.wireOp",EDGE,"E88.MirrorC")}),1.0]])]});
            extrude(context, id + "F17", {"entities" : qUnion([Q0, Q1, Q2]), "depth" : 25 * mm});
        }
    });
